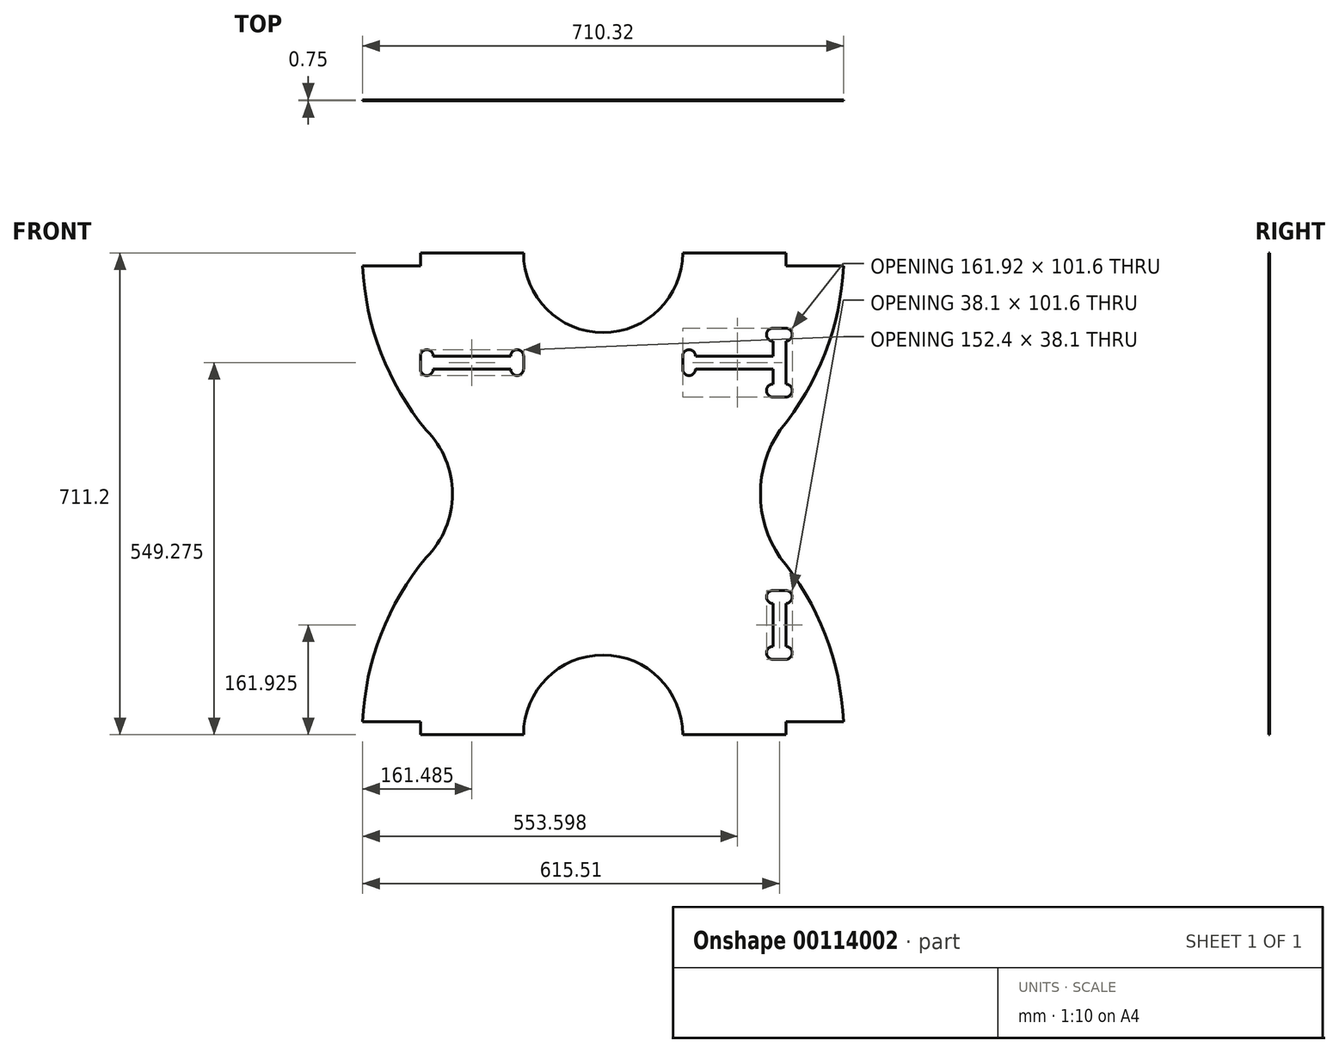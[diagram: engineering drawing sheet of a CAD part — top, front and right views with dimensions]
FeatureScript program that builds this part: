
annotation { "Feature Type Name" : "Feature", "Feature Type Description" : "" }
export const myFeature = defineFeature(function(context is Context, id is Id, definition is map)
    precondition{}
    {
        {
            assignVariable(context, id + "F0", {"name" : "thickness", "anyValue" : 3 / 4});
        }
        {
            var Q0;
            Q0=qCreatedBy(makeId("Front.planeOp"),FACE);
            var sketch = newSketch(context, id + "F1", { "sketchPlane" : qUnion([Q0])});
            skLineSegment(sketch, "E0.bottom", {"start": v(-355.6, 355.6) * mm, "end": v(355.6, 355.6) * mm, "construction": true});
            skLineSegment(sketch, "E0.top", {"start": v(-355.6, -355.6) * mm, "end": v(355.6, -355.6) * mm, "construction": true});
            skLineSegment(sketch, "E0.left", {"start": v(-355.6, 355.6) * mm, "end": v(-355.6, -355.6) * mm, "construction": true});
            skPoint(sketch, "E1", {"position": v(-355.6, 0) * mm});
            skPoint(sketch, "E2", {"position": v(0, 355.6) * mm});
            skLineSegment(sketch, "E3.bottom", {"start": v(203.2, 355.6) * mm, "end": v(-203.2, 355.6) * mm});
            skLineSegment(sketch, "E3.top", {"start": v(203.2, 336.55) * mm, "end": v(-203.2, 336.55) * mm, "construction": true});
            skLineSegment(sketch, "E3.left", {"start": v(203.2, 355.6) * mm, "end": v(203.2, 336.55) * mm});
            skLineSegment(sketch, "E3.right", {"start": v(-203.2, 355.6) * mm, "end": v(-203.2, 336.55) * mm});
            skLineSegment(sketch, "E4.bottom", {"start": v(-203.2, -355.6) * mm, "end": v(203.2, -355.6) * mm});
            skLineSegment(sketch, "E4.top", {"start": v(-203.2, -396.88) * mm, "end": v(203.2, -396.88) * mm, "construction": true});
            skLineSegment(sketch, "E4.left", {"start": v(-203.2, -396.88) * mm, "end": v(-203.2, -355.6) * mm});
            skLineSegment(sketch, "E4.right", {"start": v(203.2, -396.88) * mm, "end": v(203.2, -355.6) * mm});
            skCircle(sketch, "E5", {"center": v(-355.6, 0) * mm, "radius": 133.16 * mm, "construction": true});
            skArc(sketch, "E6", {"start": v(-355.6, 355.6) * mm, "mid": v(-331.34, 216.66) * mm, "end": v(-261.44, 94.16) * mm});
            skLineSegment(sketch, "E7", {"start": v(-355.6, 0) * mm, "end": v(-261.44, 94.16) * mm, "construction": true});
            skLineSegment(sketch, "E8", {"start": v(0, 355.6) * mm, "end": v(0, -355.6) * mm, "construction": true});
            skLineSegment(sketch, "E9", {"start": v(558.8, 0) * mm, "end": v(-355.6, 0) * mm, "construction": true});
            skArc(sketch, "E10.MirrorCS", {"start": v(-355.6, -355.6) * mm, "mid": v(-331.34, -216.66) * mm, "end": v(-261.44, -94.16) * mm});
            skArc(sketch, "E11.MirrorCS", {"start": v(355.6, -355.6) * mm, "mid": v(331.34, -216.66) * mm, "end": v(261.44, -94.16) * mm});
            skCircle(sketch, "E12.MirrorC", {"center": v(355.6, 0) * mm, "radius": 133.16 * mm, "construction": true});
            skArc(sketch, "E13.MirrorCS", {"start": v(355.6, 355.6) * mm, "mid": v(331.34, 216.66) * mm, "end": v(261.44, 94.16) * mm});
            skLineSegment(sketch, "E14", {"start": v(-355.6, 355.6) * mm, "end": v(-203.2, 355.6) * mm});
            skLineSegment(sketch, "E15", {"start": v(203.2, 355.6) * mm, "end": v(355.6, 355.6) * mm});
            skLineSegment(sketch, "E16", {"start": v(355.6, -355.6) * mm, "end": v(203.2, -355.6) * mm});
            skLineSegment(sketch, "E17", {"start": v(-203.2, -355.6) * mm, "end": v(-355.6, -355.6) * mm});
            skArc(sketch, "E18", {"start": v(-261.44, -94.16) * mm, "mid": v(-222.38, 0) * mm, "end": v(-261.44, 94.16) * mm});
            skArc(sketch, "E19", {"start": v(261.44, 94.16) * mm, "mid": v(232.4, 0) * mm, "end": v(261.44, -94.16) * mm});
            skSolve(sketch);
        }
        {
            var Q0;
            Q0 = qSketchRegion(id + "F1", true);
            extrude(context, id + "F2", {"entities" : qUnion([Q0]), "depth" : (getVariable(context, 'thickness')) * mm});
        }
        {
            var Q0;
            Q0=makeQuery(id+"F2.opExtrude","CAP_FACE",FACE,{"disambiguationData":[OSD([sQuery(id+"F1.wireOp",EDGE,"E3.bottom"),sQuery(id+"F1.wireOp",EDGE,"E6"),sQuery(id+"F1.wireOp",EDGE,"E10.MirrorCS"),sQuery(id+"F1.wireOp",EDGE,"E11.MirrorCS"),sQuery(id+"F1.wireOp",EDGE,"E13.MirrorCS"),sQuery(id+"F1.wireOp",EDGE,"E14"),sQuery(id+"F1.wireOp",EDGE,"E15"),sQuery(id+"F1.wireOp",EDGE,"E16"),sQuery(id+"F1.wireOp",EDGE,"E17"),sQuery(id+"F1.wireOp",EDGE,"E18"),sQuery(id+"F1.wireOp",EDGE,"E19"),sQuery(id+"F1.wireOp",EDGE,"E4.bottom")])],"isStart":false});
            var sketch = newSketch(context, id + "F3", { "sketchPlane" : qUnion([Q0])});
            skLineSegment(sketch, "E20.bottom", {"start": v(-355.6, 355.6) * mm, "end": v(-269.87, 355.6) * mm});
            skLineSegment(sketch, "E20.top", {"start": v(-355.6, 336.55) * mm, "end": v(-269.87, 336.55) * mm});
            skLineSegment(sketch, "E20.left", {"start": v(-355.6, 355.6) * mm, "end": v(-355.6, 336.55) * mm});
            skLineSegment(sketch, "E20.right", {"start": v(-269.87, 355.6) * mm, "end": v(-269.87, 336.55) * mm});
            skLineSegment(sketch, "E21", {"start": v(0, 355.6) * mm, "end": v(0, -355.6) * mm, "construction": true});
            skPoint(sketch, "E22", {"position": v(0, 0) * mm});
            skLineSegment(sketch, "E23", {"start": v(0, 0) * mm, "end": v(226.28, 0) * mm, "construction": true});
            skLineSegment(sketch, "E24.MirrorCS", {"start": v(269.87, 355.6) * mm, "end": v(269.87, 336.55) * mm});
            skLineSegment(sketch, "E25.MirrorCS", {"start": v(355.6, 336.55) * mm, "end": v(269.87, 336.55) * mm});
            skLineSegment(sketch, "E26.MirrorCS", {"start": v(355.6, 355.6) * mm, "end": v(269.87, 355.6) * mm});
            skLineSegment(sketch, "E27.MirrorCS", {"start": v(355.6, 355.6) * mm, "end": v(355.6, 336.55) * mm});
            skLineSegment(sketch, "E28.MirrorCS", {"start": v(355.6, -355.6) * mm, "end": v(355.6, -336.55) * mm});
            skLineSegment(sketch, "E29.MirrorCS", {"start": v(269.87, -355.6) * mm, "end": v(269.87, -336.55) * mm});
            skLineSegment(sketch, "E30.MirrorCS", {"start": v(-269.87, -355.6) * mm, "end": v(-269.87, -336.55) * mm});
            skLineSegment(sketch, "E31.MirrorCS", {"start": v(-355.6, -355.6) * mm, "end": v(-355.6, -336.55) * mm});
            skLineSegment(sketch, "E32.MirrorCS", {"start": v(-355.6, -336.55) * mm, "end": v(-269.87, -336.55) * mm});
            skLineSegment(sketch, "E33.MirrorCS", {"start": v(-355.6, -355.6) * mm, "end": v(-269.87, -355.6) * mm});
            skLineSegment(sketch, "E34.MirrorCS", {"start": v(355.6, -336.55) * mm, "end": v(269.87, -336.55) * mm});
            skLineSegment(sketch, "E35.MirrorCS", {"start": v(355.6, -355.6) * mm, "end": v(269.87, -355.6) * mm});
            skCircle(sketch, "E36", {"center": v(0, 355.6) * mm, "radius": 117.47 * mm});
            skCircle(sketch, "E37.MirrorC", {"center": v(0, -355.6) * mm, "radius": 117.47 * mm});
            skSolve(sketch);
        }
        {
            var Q0;
            Q0 = qSketchRegion(id + "F3", true);
            extrude(context, id + "F4", {"entities" : qUnion([Q0]), "operationType" : NewBodyOperationType.REMOVE, "oppositeDirection" : true, "depth" : 25.4 * mm});
        }
        {
            var Q0;
            Q0=makeQuery(id+"F2.opExtrude","CAP_FACE",FACE,{"disambiguationData":[OSD([sQuery(id+"F1.wireOp",EDGE,"E3.bottom"),sQuery(id+"F1.wireOp",EDGE,"E6"),sQuery(id+"F1.wireOp",EDGE,"E10.MirrorCS"),sQuery(id+"F1.wireOp",EDGE,"E11.MirrorCS"),sQuery(id+"F1.wireOp",EDGE,"E13.MirrorCS"),sQuery(id+"F1.wireOp",EDGE,"E14"),sQuery(id+"F1.wireOp",EDGE,"E15"),sQuery(id+"F1.wireOp",EDGE,"E16"),sQuery(id+"F1.wireOp",EDGE,"E17"),sQuery(id+"F1.wireOp",EDGE,"E18"),sQuery(id+"F1.wireOp",EDGE,"E19"),sQuery(id+"F1.wireOp",EDGE,"E4.bottom")])],"isStart":false});
            var sketch = newSketch(context, id + "F5", { "sketchPlane" : qUnion([Q0])});
            skLineSegment(sketch, "E38.bottom", {"start": v(-269.87, 203.2) * mm, "end": v(-117.47, 203.2) * mm});
            skLineSegment(sketch, "E38.top", {"start": v(-269.87, 184.15) * mm, "end": v(-117.47, 184.15) * mm});
            skLineSegment(sketch, "E38.left", {"start": v(-269.87, 203.2) * mm, "end": v(-269.87, 184.15) * mm});
            skLineSegment(sketch, "E38.right", {"start": v(-117.47, 203.2) * mm, "end": v(-117.47, 184.15) * mm});
            skPoint(sketch, "E39", {"position": v(-117.47, 355.6) * mm});
            skLineSegment(sketch, "E40", {"start": v(-117.47, 355.6) * mm, "end": v(-117.47, 23.64) * mm, "construction": true});
            skLineSegment(sketch, "E41", {"start": v(0, 0) * mm, "end": v(0, 108.99) * mm, "construction": true});
            skLineSegment(sketch, "E42", {"start": v(0, 108.99) * mm, "end": v(0, 0) * mm, "construction": true});
            skLineSegment(sketch, "E43", {"start": v(78.73, 0) * mm, "end": v(0, 0) * mm, "construction": true});
            skLineSegment(sketch, "E44.MirrorCS", {"start": v(117.47, 203.2) * mm, "end": v(117.47, 184.15) * mm});
            skLineSegment(sketch, "E45.MirrorCS", {"start": v(269.87, 203.2) * mm, "end": v(269.87, 184.15) * mm});
            skLineSegment(sketch, "E46.MirrorCS", {"start": v(269.87, 184.15) * mm, "end": v(117.47, 184.15) * mm});
            skLineSegment(sketch, "E47.MirrorCS", {"start": v(269.87, 203.2) * mm, "end": v(117.47, 203.2) * mm});
            skSolve(sketch);
        }
        {
            var Q0;
            Q0 = qSketchRegion(id + "F5", true);
            extrude(context, id + "F6", {"entities" : qUnion([Q0]), "operationType" : NewBodyOperationType.REMOVE, "oppositeDirection" : true, "depth" : 25.4 * mm});
        }
        {
            var Q0;
            Q0=makeQuery(id+"F2.opExtrude","CAP_FACE",FACE,{"disambiguationData":[OSD([sQuery(id+"F1.wireOp",EDGE,"E3.bottom"),sQuery(id+"F1.wireOp",EDGE,"E6"),sQuery(id+"F1.wireOp",EDGE,"E10.MirrorCS"),sQuery(id+"F1.wireOp",EDGE,"E11.MirrorCS"),sQuery(id+"F1.wireOp",EDGE,"E13.MirrorCS"),sQuery(id+"F1.wireOp",EDGE,"E14"),sQuery(id+"F1.wireOp",EDGE,"E15"),sQuery(id+"F1.wireOp",EDGE,"E16"),sQuery(id+"F1.wireOp",EDGE,"E17"),sQuery(id+"F1.wireOp",EDGE,"E18"),sQuery(id+"F1.wireOp",EDGE,"E19"),sQuery(id+"F1.wireOp",EDGE,"E4.bottom")])],"isStart":false});
            var sketch = newSketch(context, id + "F7", { "sketchPlane" : qUnion([Q0])});
            skArc(sketch, "E48", {"start": v(-250.82, 203.2) * mm, "mid": v(-260.35, 212.73) * mm, "end": v(-269.87, 203.2) * mm});
            skArc(sketch, "E49", {"start": v(-269.87, 184.15) * mm, "mid": v(-260.35, 174.63) * mm, "end": v(-250.82, 184.15) * mm});
            skLineSegment(sketch, "E50", {"start": v(-269.87, 203.2) * mm, "end": v(-269.87, 184.15) * mm});
            skLineSegment(sketch, "E51", {"start": v(-250.82, 203.2) * mm, "end": v(-250.82, 184.15) * mm});
            skLineSegment(sketch, "E52", {"start": v(-193.67, 203.2) * mm, "end": v(-193.67, 184.15) * mm, "construction": true});
            skLineSegment(sketch, "E53.MirrorCS", {"start": v(-136.52, 203.2) * mm, "end": v(-136.52, 184.15) * mm});
            skLineSegment(sketch, "E54.MirrorCS", {"start": v(-117.47, 203.2) * mm, "end": v(-117.47, 184.15) * mm});
            skArc(sketch, "E55.MirrorCS", {"start": v(-117.47, 184.15) * mm, "mid": v(-127, 174.63) * mm, "end": v(-136.52, 184.15) * mm});
            skArc(sketch, "E56.MirrorCS", {"start": v(-136.52, 203.2) * mm, "mid": v(-127, 212.73) * mm, "end": v(-117.47, 203.2) * mm});
            skLineSegment(sketch, "E57", {"start": v(0, 72.44) * mm, "end": v(0, 0) * mm, "construction": true});
            skArc(sketch, "E58.MirrorCS", {"start": v(117.47, 184.15) * mm, "mid": v(127, 174.63) * mm, "end": v(136.52, 184.15) * mm});
            skLineSegment(sketch, "E59.MirrorCS", {"start": v(117.47, 203.2) * mm, "end": v(117.47, 184.15) * mm});
            skArc(sketch, "E60.MirrorCS", {"start": v(136.52, 203.2) * mm, "mid": v(127, 212.73) * mm, "end": v(117.47, 203.2) * mm});
            skLineSegment(sketch, "E61.MirrorCS", {"start": v(136.52, 203.2) * mm, "end": v(136.52, 184.15) * mm});
            skLineSegment(sketch, "E62.MirrorCS", {"start": v(250.82, 203.2) * mm, "end": v(250.82, 184.15) * mm});
            skLineSegment(sketch, "E63.MirrorCS", {"start": v(269.87, 203.2) * mm, "end": v(269.87, 184.15) * mm});
            skArc(sketch, "E64.MirrorCS", {"start": v(269.87, 184.15) * mm, "mid": v(260.35, 174.63) * mm, "end": v(250.82, 184.15) * mm});
            skArc(sketch, "E65.MirrorCS", {"start": v(250.82, 203.2) * mm, "mid": v(260.35, 212.73) * mm, "end": v(269.87, 203.2) * mm});
            skSolve(sketch);
        }
        {
            var Q0;
            Q0 = qSketchRegion(id + "F7", true);
            extrude(context, id + "F8", {"entities" : qUnion([Q0]), "operationType" : NewBodyOperationType.REMOVE, "oppositeDirection" : true, "depth" : 25.4 * mm});
        }
        {
            var Q0;
            Q0=makeQuery(id+"F2.opExtrude","CAP_FACE",FACE,{"disambiguationData":[OSD([sQuery(id+"F1.wireOp",EDGE,"E3.bottom"),sQuery(id+"F1.wireOp",EDGE,"E6"),sQuery(id+"F1.wireOp",EDGE,"E10.MirrorCS"),sQuery(id+"F1.wireOp",EDGE,"E11.MirrorCS"),sQuery(id+"F1.wireOp",EDGE,"E13.MirrorCS"),sQuery(id+"F1.wireOp",EDGE,"E14"),sQuery(id+"F1.wireOp",EDGE,"E15"),sQuery(id+"F1.wireOp",EDGE,"E16"),sQuery(id+"F1.wireOp",EDGE,"E17"),sQuery(id+"F1.wireOp",EDGE,"E18"),sQuery(id+"F1.wireOp",EDGE,"E19"),sQuery(id+"F1.wireOp",EDGE,"E4.bottom")])],"isStart":false});
            var sketch = newSketch(context, id + "F9", { "sketchPlane" : qUnion([Q0])});
            skLineSegment(sketch, "E66.bottom", {"start": v(250.82, 244.48) * mm, "end": v(269.87, 244.48) * mm});
            skLineSegment(sketch, "E66.top", {"start": v(250.82, 142.88) * mm, "end": v(269.87, 142.88) * mm});
            skLineSegment(sketch, "E66.left", {"start": v(250.82, 244.48) * mm, "end": v(250.82, 142.88) * mm});
            skLineSegment(sketch, "E66.right", {"start": v(269.87, 244.48) * mm, "end": v(269.87, 142.88) * mm});
            skLineSegment(sketch, "E67", {"start": v(260.35, 244.48) * mm, "end": v(260.35, 142.88) * mm, "construction": true});
            skLineSegment(sketch, "E68", {"start": v(117.47, 193.68) * mm, "end": v(269.87, 193.68) * mm, "construction": true});
            skLineSegment(sketch, "E69", {"start": v(0, 0) * mm, "end": v(466.56, 0) * mm, "construction": true});
            skPoint(sketch, "E69.endSnap0", {"position": v(232.4, 0) * mm});
            skLineSegment(sketch, "E70.MirrorCS", {"start": v(250.83, -244.48) * mm, "end": v(269.87, -244.48) * mm});
            skLineSegment(sketch, "E71.MirrorCS", {"start": v(250.83, -142.88) * mm, "end": v(269.87, -142.88) * mm});
            skLineSegment(sketch, "E72.MirrorCS", {"start": v(269.87, -244.48) * mm, "end": v(269.87, -142.88) * mm});
            skLineSegment(sketch, "E73.MirrorCS", {"start": v(250.82, -244.48) * mm, "end": v(250.82, -142.88) * mm});
            skPoint(sketch, "E74", {"position": v(260.35, 193.68) * mm});
            skPoint(sketch, "E75", {"position": v(193.67, 193.68) * mm});
            skSolve(sketch);
        }
        {
            var Q0;
            Q0 = qSketchRegion(id + "F9", true);
            extrude(context, id + "F10", {"entities" : qUnion([Q0]), "operationType" : NewBodyOperationType.REMOVE, "oppositeDirection" : true, "depth" : 25.4 * mm});
        }
        {
            var Q0;
            Q0=makeQuery(id+"F2.opExtrude","CAP_FACE",FACE,{"disambiguationData":[OSD([sQuery(id+"F1.wireOp",EDGE,"E3.bottom"),sQuery(id+"F1.wireOp",EDGE,"E6"),sQuery(id+"F1.wireOp",EDGE,"E10.MirrorCS"),sQuery(id+"F1.wireOp",EDGE,"E11.MirrorCS"),sQuery(id+"F1.wireOp",EDGE,"E13.MirrorCS"),sQuery(id+"F1.wireOp",EDGE,"E14"),sQuery(id+"F1.wireOp",EDGE,"E15"),sQuery(id+"F1.wireOp",EDGE,"E16"),sQuery(id+"F1.wireOp",EDGE,"E17"),sQuery(id+"F1.wireOp",EDGE,"E18"),sQuery(id+"F1.wireOp",EDGE,"E19"),sQuery(id+"F1.wireOp",EDGE,"E4.bottom")])],"isStart":false});
            var sketch = newSketch(context, id + "F11", { "sketchPlane" : qUnion([Q0])});
            skArc(sketch, "E76", {"start": v(250.82, 244.48) * mm, "mid": v(241.3, 234.95) * mm, "end": v(250.82, 225.43) * mm});
            skArc(sketch, "E77", {"start": v(269.87, 225.42) * mm, "mid": v(279.4, 234.95) * mm, "end": v(269.87, 244.48) * mm});
            skLineSegment(sketch, "E78", {"start": v(250.82, 244.47) * mm, "end": v(269.87, 244.48) * mm});
            skLineSegment(sketch, "E79", {"start": v(269.87, 225.43) * mm, "end": v(250.82, 225.43) * mm});
            skLineSegment(sketch, "E80", {"start": v(117.47, 193.67) * mm, "end": v(269.87, 193.68) * mm, "construction": true});
            skArc(sketch, "E81.MirrorCS", {"start": v(269.87, 161.93) * mm, "mid": v(279.4, 152.4) * mm, "end": v(269.87, 142.87) * mm});
            skLineSegment(sketch, "E82.MirrorCS", {"start": v(250.82, 142.88) * mm, "end": v(269.87, 142.88) * mm});
            skLineSegment(sketch, "E83.MirrorCS", {"start": v(269.87, 161.93) * mm, "end": v(250.82, 161.93) * mm});
            skArc(sketch, "E84.MirrorCS", {"start": v(250.82, 142.88) * mm, "mid": v(241.3, 152.4) * mm, "end": v(250.82, 161.93) * mm});
            skLineSegment(sketch, "E85", {"start": v(0, 0) * mm, "end": v(485.15, 0) * mm, "construction": true});
            skLineSegment(sketch, "E86.MirrorCS", {"start": v(250.82, -142.88) * mm, "end": v(269.87, -142.88) * mm});
            skArc(sketch, "E87.MirrorCS", {"start": v(250.82, -142.88) * mm, "mid": v(241.3, -152.4) * mm, "end": v(250.82, -161.93) * mm});
            skArc(sketch, "E88.MirrorCS", {"start": v(269.87, -161.93) * mm, "mid": v(279.4, -152.4) * mm, "end": v(269.87, -142.87) * mm});
            skLineSegment(sketch, "E89.MirrorCS", {"start": v(269.87, -161.93) * mm, "end": v(250.82, -161.93) * mm});
            skLineSegment(sketch, "E90.MirrorCS", {"start": v(250.82, -244.47) * mm, "end": v(269.87, -244.47) * mm});
            skLineSegment(sketch, "E91.MirrorCS", {"start": v(269.87, -225.43) * mm, "end": v(250.82, -225.43) * mm});
            skArc(sketch, "E92.MirrorCS", {"start": v(250.82, -244.48) * mm, "mid": v(241.3, -234.95) * mm, "end": v(250.82, -225.43) * mm});
            skArc(sketch, "E93.MirrorCS", {"start": v(269.87, -225.42) * mm, "mid": v(279.4, -234.95) * mm, "end": v(269.87, -244.48) * mm});
            skSolve(sketch);
        }
        {
            var Q0;
            Q0 = qSketchRegion(id + "F11", true);
            extrude(context, id + "F12", {"entities" : qUnion([Q0]), "operationType" : NewBodyOperationType.REMOVE, "oppositeDirection" : true, "depth" : 25.4 * mm});
        }
    });
